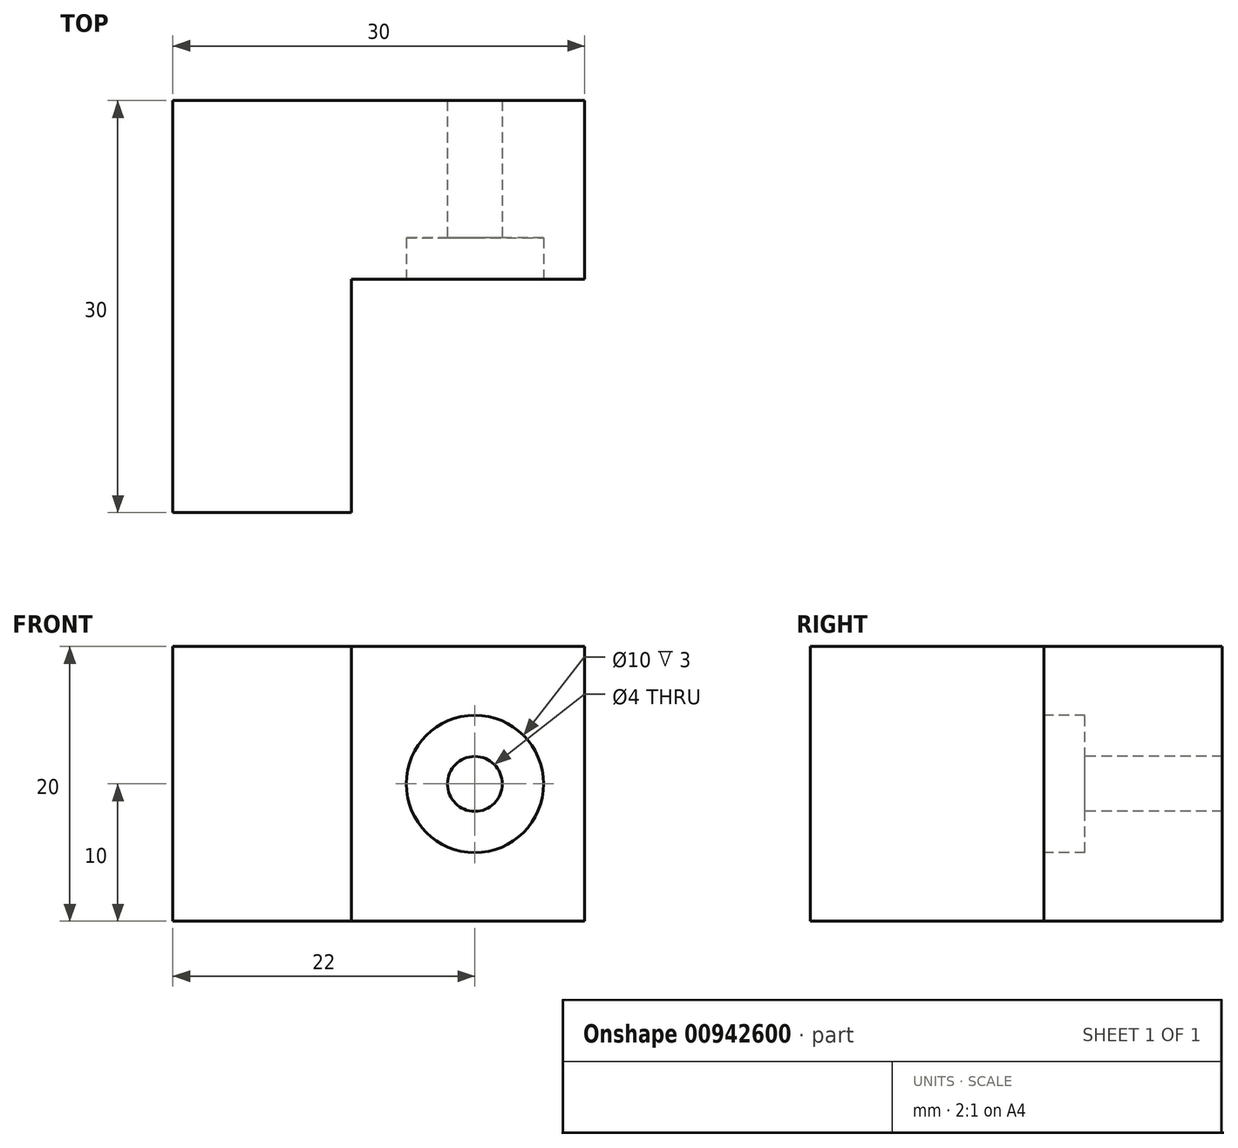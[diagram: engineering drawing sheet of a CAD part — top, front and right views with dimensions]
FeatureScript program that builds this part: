
annotation { "Feature Type Name" : "Feature", "Feature Type Description" : "" }
export const myFeature = defineFeature(function(context is Context, id is Id, definition is map)
    precondition{}
    {
        {
            var Q0;
            Q0=qCreatedBy(makeId("Top.planeOp"),FACE);
            var sketch = newSketch(context, id + "F0", { "sketchPlane" : qUnion([Q0])});
            skLineSegment(sketch, "E0", {"start": v(0, 0) * mm, "end": v(30, 0) * mm});
            skLineSegment(sketch, "E1", {"start": v(30, 0) * mm, "end": v(30, -13) * mm});
            skLineSegment(sketch, "E2", {"start": v(30, -13) * mm, "end": v(13, -13) * mm});
            skLineSegment(sketch, "E3", {"start": v(13, -13) * mm, "end": v(13, -30) * mm});
            skLineSegment(sketch, "E4", {"start": v(13, -30) * mm, "end": v(0, -30) * mm});
            skLineSegment(sketch, "E5", {"start": v(0, -30) * mm, "end": v(0, 0) * mm});
            skSolve(sketch);
        }
        {
            var Q0;
            Q0 = qSketchRegion(id + "F0", true);
            extrude(context, id + "F1", {"entities" : qUnion([Q0]), "depth" : 20 * mm, "offsetDistance" : 25 * mm});
        }
        {
            var Q0;
            Q0=makeQuery(id+"F1.opExtrude","SWEPT_FACE",FACE,{"disambiguationData":[OSD([sQuery(id+"F0.wireOp",EDGE,"E2")])]});
            var sketch = newSketch(context, id + "F2", { "sketchPlane" : qUnion([Q0])});
            skCircle(sketch, "E6", {"center": v(22, 10) * mm, "radius": 5 * mm});
            skSolve(sketch);
        }
        {
            var Q0;
            Q0 = qSketchRegion(id + "F2", true);
            extrude(context, id + "F3", {"entities" : qUnion([Q0]), "operationType" : NewBodyOperationType.REMOVE, "oppositeDirection" : true, "depth" : 3 * mm, "offsetDistance" : 25 * mm});
        }
        {
            var Q0;
            Q0=makeQuery(id+"F3.boolean.opBoolean","COPY",FACE,{"derivedFrom":makeQuery(id+"F3.opExtrude","CAP_FACE",FACE,{"disambiguationData":[OSD([sQuery(id+"F2.wireOp",EDGE,"E6")])],"isStart":false})});
            var sketch = newSketch(context, id + "F4", { "sketchPlane" : qUnion([Q0])});
            skCircle(sketch, "E7", {"center": v(22, 10) * mm, "radius": 2 * mm});
            skSolve(sketch);
        }
        {
            var Q0;
            Q0 = qSketchRegion(id + "F4", true);
            extrude(context, id + "F5", {"entities" : qUnion([Q0]), "operationType" : NewBodyOperationType.REMOVE, "endBound" : BoundingType.UP_TO_NEXT, "oppositeDirection" : true, "depth" : 25 * mm, "offsetDistance" : 25 * mm});
        }
        {
            var Q0;
            Q0=makeQuery(id+"F1.opExtrude","CAP_VERTEX",VERTEX,{"disambiguationData":[OSD([sQuery(id+"F0.wireOp",EDGE,"E2"),sQuery(id+"F0.wireOp",EDGE,"E3")])],"isStart":true});
            var Q1;
            Q1=qCreatedBy(makeId("Origin.pointOp"),VERTEX);
            var Q2;
            Q2=makeQuery(id+"F1.opExtrude","CAP_VERTEX",VERTEX,{"disambiguationData":[OSD([sQuery(id+"F0.wireOp",EDGE,"E0"),sQuery(id+"F0.wireOp",EDGE,"E5")])],"isStart":false});
            cPlane(context, id + "F6", {"entities" : qUnion([Q0, Q1, Q2]), "cplaneType" : CPlaneType.THREE_POINT, "offset" : 25 * mm, "width" : 150 * mm, "height" : 150 * mm});
        }
    });
